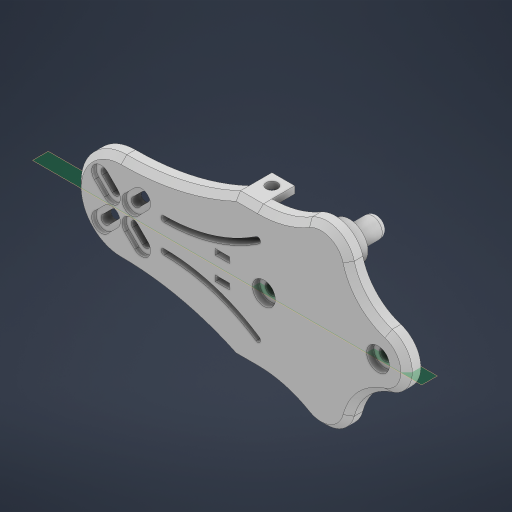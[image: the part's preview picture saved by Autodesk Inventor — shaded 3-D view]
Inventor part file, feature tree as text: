
AUTODESK INVENTOR PART (.ipt)
format: ipt  version: 2024.2 (Build 282272000, 272)  size: 1,128,448 bytes
history: native  units: in
note: dims shown in document units (in); Inventor stores cm internally (conversion verified against a paired STEP export)
features: extrude x15, sketch x14, projected_geometry x10, mirror x4, fillet x2, plane x1, revolve x1, chamfer x1
ambient origin geometry x8: Origin, YZ Plane, XZ Plane, XY Plane, X Axis, Y Axis, Z Axis, Center Point
bodies: Solid1 (feature_tree)
feature tree (48):
  extrude  "Extrusion1"  Depth=2.3441in
  plane  "Work Plane1"
  extrude  "Extrusion3"  Depth=0.1575in
  mirror  "Mirror1"
  extrude  "Extrusion4"  Depth=0.3677in
  extrude  "Extrusion5"  Depth=0.3937in
  mirror  "Mirror2"
  sketch  "Sketch7"  dims[d18=0.315in d19=0.5906in]
  extrude  "Extrusion6"  Depth=0.5906in
  extrude  "Extrusion7"  TaperAngle=0.0deg  [1 undecoded]
  extrude  "Extrusion8"  Depth=0.0984in
  fillet  "Fillet1"  Radius=0.315in
  extrude  "Extrusion9"  Depth=0.1575in
  mirror  "Mirror3"
  extrude  "Extrusion10"  Depth=0.7874in
  revolve  "Revolution1"  [1 undecoded]
  extrude  "Extrusion11"  Depth=0.1969in TaperAngle=0.0deg
  mirror  "Mirror4"
  extrude  "Extrusion12"  Depth=0.3937in TaperAngle=0.0deg
  fillet  "Fillet2"  Radius=0.0787in
  extrude  "Extrusion14"  Depth=0.6299in
  sketch  "Sketch17"  dims[d45=3.9135in d46=0.1181in d47=0.315in d48=45.0deg d49=0.0974in d50=1.5748in d52=360.0deg d54=0.2362in d55=0.3937in d56=1.378in d57=0.0787in d58=0.0in d59=0.1181in d60=90.0deg d61=0.0787in d62=0.1969in d63=0.2756in d64=0.0in d65=0.0in d66=0.0689in d67=0.0591in d68=0.0in d69=0.315in d70=0.0984in d71=0.0in d72=0.0787in d73=0.0787in d74=0.0787in d75=45.0deg d76=1.1811in d77=0.7874in d78=0.2362in d79=2.3622in d80=1.5748in d81=0.0in d82=0.0in d83=0.7874in d84=0.7874in d85=0.7874in d86=0.7874in d87=0.7874in d88=0.3937in d89=0.0in d90=0.0in d91=0.0in]
  extrude  "Extrusion15"  Depth=0.3937in
  extrude  "Extrusion16"  Depth=0.3937in
  extrude  "Extrusion13"  TaperAngle=45.0deg  [1 undecoded]
  chamfer  "Chamfer1"  Distance=0.0974in
  sketch  "Sketch1"  dims[d3=1.9685in d4=2.3441in]
  sketch  "Sketch4"  dims[d5=0.1969in d6=0.0in d12=0.1575in]
  sketch  "Sketch5"  dims[d13=1.5748in d15=0.3677in]
  projected_geometry  "Projected Loop1"
  sketch  "Sketch6"  dims[d16=0.0787in d17=0.3937in]
  projected_geometry  "Projected Loop2"
  projected_geometry  "Projected Loop3"
  sketch  "Sketch8"  dims[d20=0.1969in d21=0.0in d22=0.0in]
  projected_geometry  "Projected Loop4"
  sketch  "Sketch9"  dims[d23=0.315in d24=0.0984in d25=0.315in d26=0.0in]
  projected_geometry  "Projected Loop5"
  sketch  "Sketch11"  dims[d27=0.1575in d28=0.1575in]
  sketch  "Sketch12"  dims[d29=0.315in d30=0.0in d31=0.7874in]
  projected_geometry  "Projected Loop6"
  sketch  "Sketch13"  dims[d32=0.8268in d33=0.3937in d34=0.0in]
  projected_geometry  "Projected Loop7"
  sketch  "Sketch14"  dims[d35=0.5118in d36=0.1969in d37=0.0in]
  projected_geometry  "Projected Loop8"
  sketch  "Sketch15"  dims[d38=0.2756in d39=0.3937in d40=0.0in d41=0.0787in]
  projected_geometry  "Projected Loop9"
  sketch  "Sketch16"  dims[d42=0.0in d43=0.0in d44=0.6299in]
  projected_geometry  "Projected Loop10"
note: 3 required parameter values undecoded (feature->parameter linkage not recoverable at this tier; creation-order binding heuristic only, values carry confidence <= 0.55)